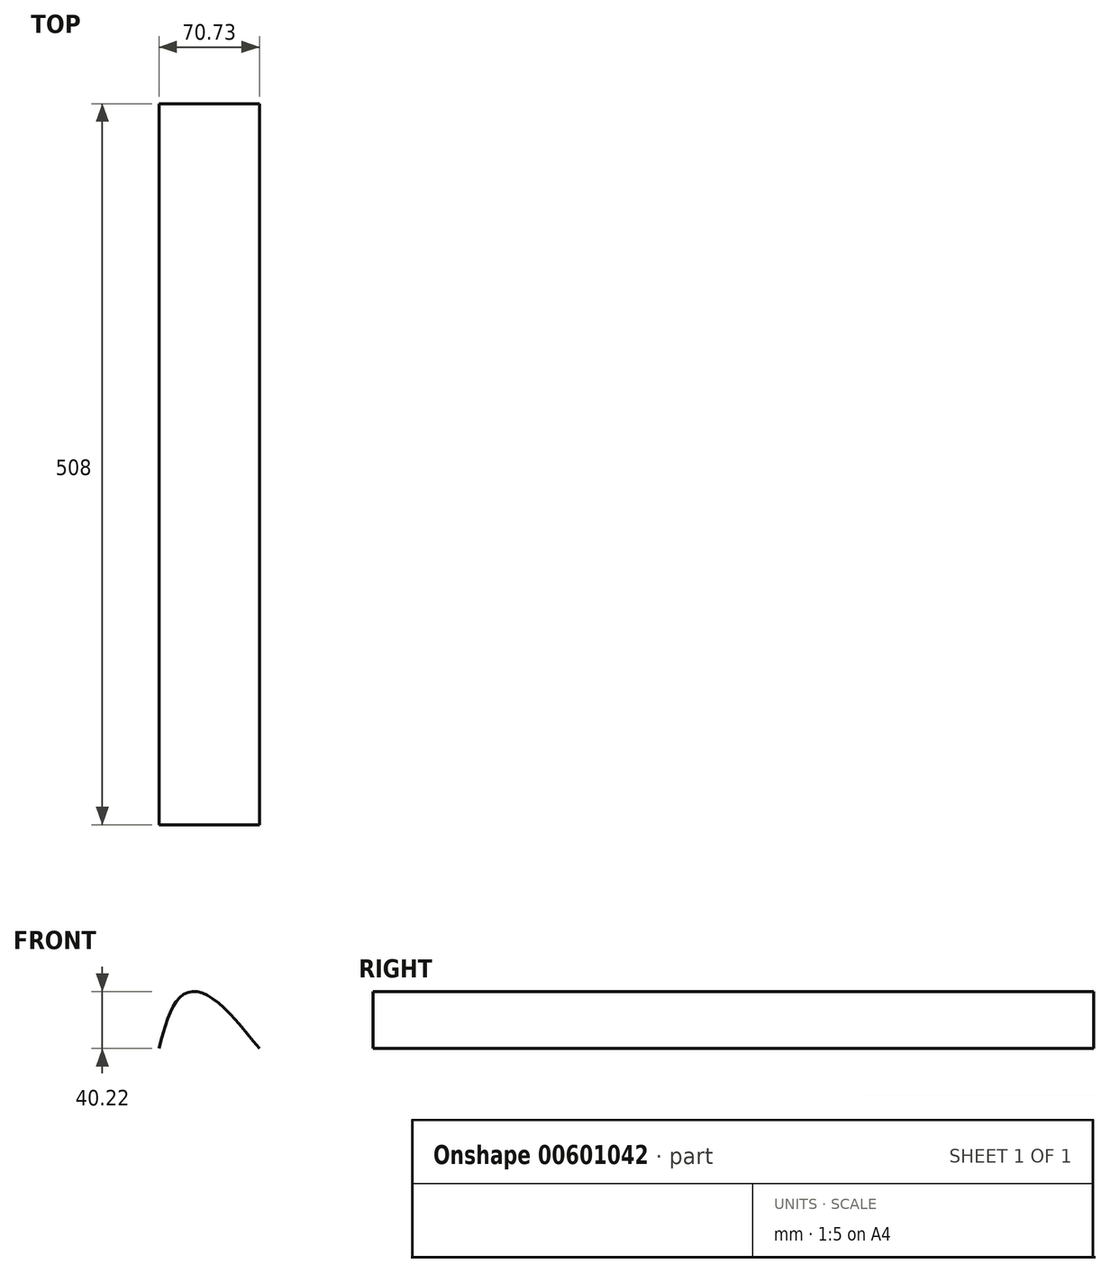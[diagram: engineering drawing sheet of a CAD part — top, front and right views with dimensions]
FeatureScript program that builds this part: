
annotation { "Feature Type Name" : "Feature", "Feature Type Description" : "" }
export const myFeature = defineFeature(function(context is Context, id is Id, definition is map)
    precondition{}
    {
        {
            var Q0;
            Q0=qCreatedBy(makeId("Front.planeOp"),FACE);
            var sketch = newSketch(context, id + "F0", { "sketchPlane" : qUnion([Q0])});
            skFitSpline(sketch, "E0", {"points": [v(0, 0) * mm, v(14.82, 36.27) * mm, v(32.17, 38.44) * mm, v(70.73, 0) * mm], "startDerivative": vector(33.4, 126.75) * mm, "endDerivative": vector(97.37, -120.4) * mm});
            skSolve(sketch);
        }
        {
            var Q0;
            Q0 = qSketchRegion(id + "F0", true);
            var Q1;
            Q1=sQuery(id+"F0.wireOp",EDGE,"E0");
            extrude(context, id + "F1", {"entities" : qUnion([Q0]), "bodyType" : ToolBodyType.SURFACE, "surfaceEntities" : qUnion([Q1]), "endBound" : BoundingType.SYMMETRIC, "depth" : 508 * mm, "offsetDistance" : 25.4 * mm});
        }
    });
